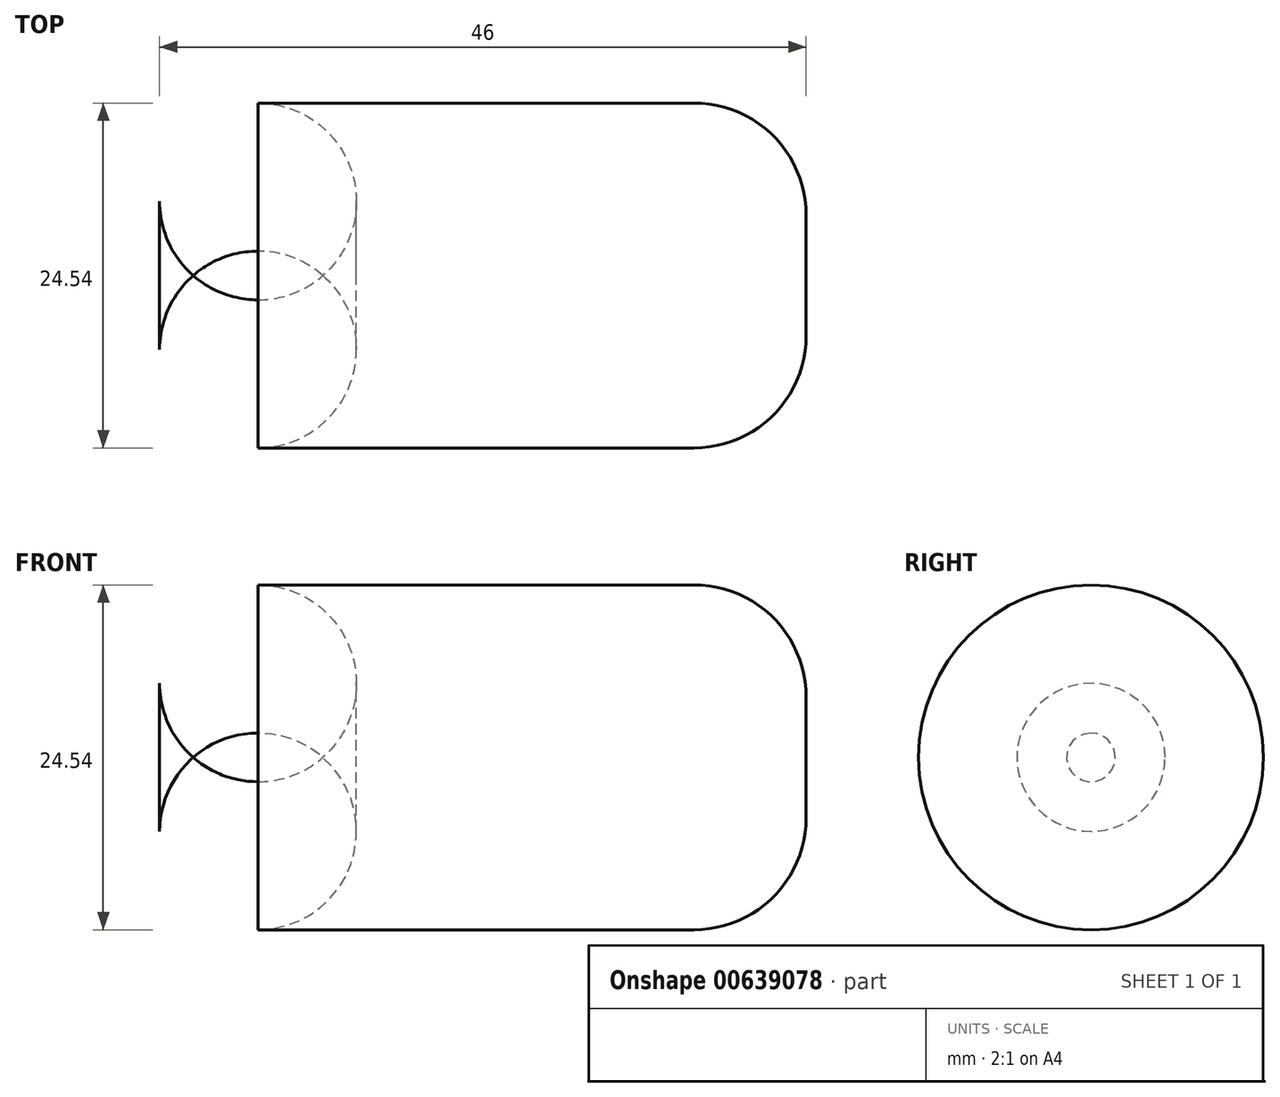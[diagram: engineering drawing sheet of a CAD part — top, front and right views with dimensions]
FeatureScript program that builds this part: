
annotation { "Feature Type Name" : "Feature", "Feature Type Description" : "" }
export const myFeature = defineFeature(function(context is Context, id is Id, definition is map)
    precondition{}
    {
        {
            var Q0;
            Q0=qCreatedBy(makeId("Right.planeOp"),FACE);
            var sketch = newSketch(context, id + "F0", { "sketchPlane" : qUnion([Q0])});
            skCircle(sketch, "E0", {"center": v(0, 0) * mm, "radius": 12.27 * mm});
            skSolve(sketch);
        }
        {
            var Q0;
            Q0 = qSketchRegion(id + "F0", true);
            extrude(context, id + "F1", {"entities" : qUnion([Q0]), "oppositeDirection" : true, "depth" : 46 * mm, "offsetDistance" : 25 * mm});
        }
        {
            var Q0;
            Q0=makeQuery(id+"F1.opExtrude","CAP_EDGE",EDGE,{"disambiguationData":[OSD([sQuery(id+"F0.wireOp",EDGE,"E0")])],"isStart":false});
            fillet(context, id + "F2", {"entities" : qUnion([Q0]), "radius" : 7 * mm, "tangentPropagation" : true, "allowEdgeOverflow" : false});
        }
        {
            var Q0;
            Q0=makeQuery(id+"F1.opExtrude","CAP_EDGE",EDGE,{"disambiguationData":[OSD([sQuery(id+"F0.wireOp",EDGE,"E0")])],"isStart":true});
            fillet(context, id + "F3", {"entities" : qUnion([Q0]), "radius" : 7.97 * mm, "tangentPropagation" : true, "allowEdgeOverflow" : false});
        }
    });
